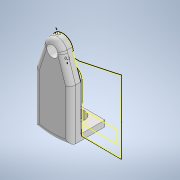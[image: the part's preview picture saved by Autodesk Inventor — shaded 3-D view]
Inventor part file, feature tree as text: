
AUTODESK INVENTOR PART (.ipt)
format: ipt  version: 2022.2 (Build 262287000, 287)  size: 183,296 bytes
history: native  units: mm
features: reference x8, sketch x5, extrude x4, other x4, plane x2, fillet x1, projected_geometry x1
ambient origin geometry x8: Origin, YZ Plane, XZ Plane, XY Plane, X Axis, Y Axis, Z Axis, Center Point
bodies: Solid1 (feature_tree)
feature tree (25):
  extrude  "Extrusion1"  Depth=1.0mm TaperAngle=0.0deg
  sketch  "Sketch2"  dims[d4=10.0mm d5=0.0mm d6=1.0mm]
  plane  "Work Plane1"
  extrude  "Extrusion2"  Depth=1.0mm
  extrude  "Extrusion3"  Depth=10.0mm
  fillet  "Fillet1"  Radius=10.0mm
  sketch  "Sketch4"
  sketch  "Sketch5"
  plane  "Work Plane2"
  extrude  "Extrusion4"  [1 undecoded]
  sketch  "Sketch1"  dims[d0=2.0mm d1=0.0mm d2=1.0mm d3=0.0mm]
  reference  "Reference1"
  reference  "Reference2"
  reference  "Reference4"
  reference  "Reference5"
  projected_geometry  "Projected Loop1"
  sketch  "Sketch3"  dims[d7=0.1mm d8=0.1mm d9=10.0mm d10=0.0mm]
  reference  "Reference6"
  reference  "Reference7"
  reference  "Reference8"
  reference  "Reference9"
  other  "<userpath>\Documents\Inventor\Wire Bender\Assembly.iam"
  other  "Assembly.iam"
  other  "Tool Head:1"
  other  "Crank:1"
note: 1 required parameter value undecoded (feature->parameter linkage not recoverable at this tier; creation-order binding heuristic only, values carry confidence <= 0.55)
